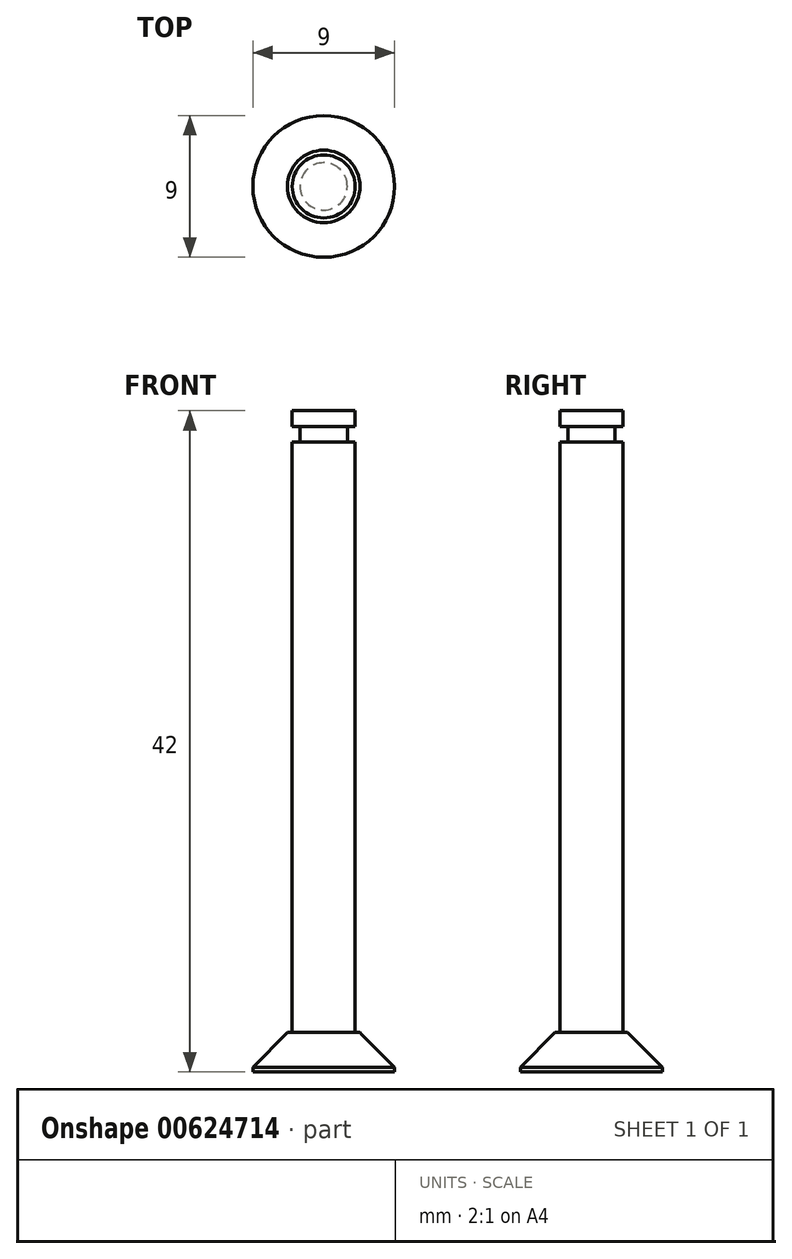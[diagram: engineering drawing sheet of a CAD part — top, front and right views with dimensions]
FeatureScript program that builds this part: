
annotation { "Feature Type Name" : "Feature", "Feature Type Description" : "" }
export const myFeature = defineFeature(function(context is Context, id is Id, definition is map)
    precondition{}
    {
        {
            var Q0;
            Q0=qCreatedBy(makeId("Front.planeOp"),FACE);
            var sketch = newSketch(context, id + "F0", { "sketchPlane" : qUnion([Q0])});
            skLineSegment(sketch, "E0", {"start": v(-4.5, 0) * mm, "end": v(0, 0) * mm});
            skLineSegment(sketch, "E1", {"start": v(0, 74.06) * mm, "end": v(0, -16.97) * mm, "construction": true});
            skLineSegment(sketch, "E2", {"start": v(-4.5, 0) * mm, "end": v(-4.5, 0.3) * mm});
            skLineSegment(sketch, "E3", {"start": v(-4.5, 0.3) * mm, "end": v(-2.3, 2.5) * mm});
            skLineSegment(sketch, "E4", {"start": v(-2.3, 2.5) * mm, "end": v(-2, 2.5) * mm});
            skLineSegment(sketch, "E5", {"start": v(-2, 2.5) * mm, "end": v(-2, 40) * mm});
            skLineSegment(sketch, "E6", {"start": v(-2, 40) * mm, "end": v(-1.5, 40) * mm});
            skLineSegment(sketch, "E7", {"start": v(-1.5, 40) * mm, "end": v(-1.5, 41) * mm});
            skLineSegment(sketch, "E8", {"start": v(-1.5, 41) * mm, "end": v(-2, 41) * mm});
            skLineSegment(sketch, "E9", {"start": v(-2, 41) * mm, "end": v(-2, 42) * mm});
            skLineSegment(sketch, "E10", {"start": v(-2, 42) * mm, "end": v(0, 42) * mm});
            skPoint(sketch, "E11.MirrorCS.end.orphan", {"position": v(0, 42) * mm});
            skLineSegment(sketch, "E12", {"start": v(0, 42) * mm, "end": v(0, 0) * mm});
            skSolve(sketch);
        }
        {
            var Q0;
            Q0=makeQuery(id+"F0.imprint","IMPRINT",FACE,{"disambiguationData":[TD([[makeQuery(id+"F0.imprint","IMPRINT",EDGE,{"derivedFrom":sQuery(id+"F0.wireOp",EDGE,"E0")}),1.0]])]});
            var Q1;
            Q1=sQuery(id+"F0.wireOp",EDGE,"E1");
            revolve(context, id + "F1", {"entities" : qUnion([Q0]), "axis" : qUnion([Q1]), "revolveType" : RevolveType.FULL});
        }
    });
